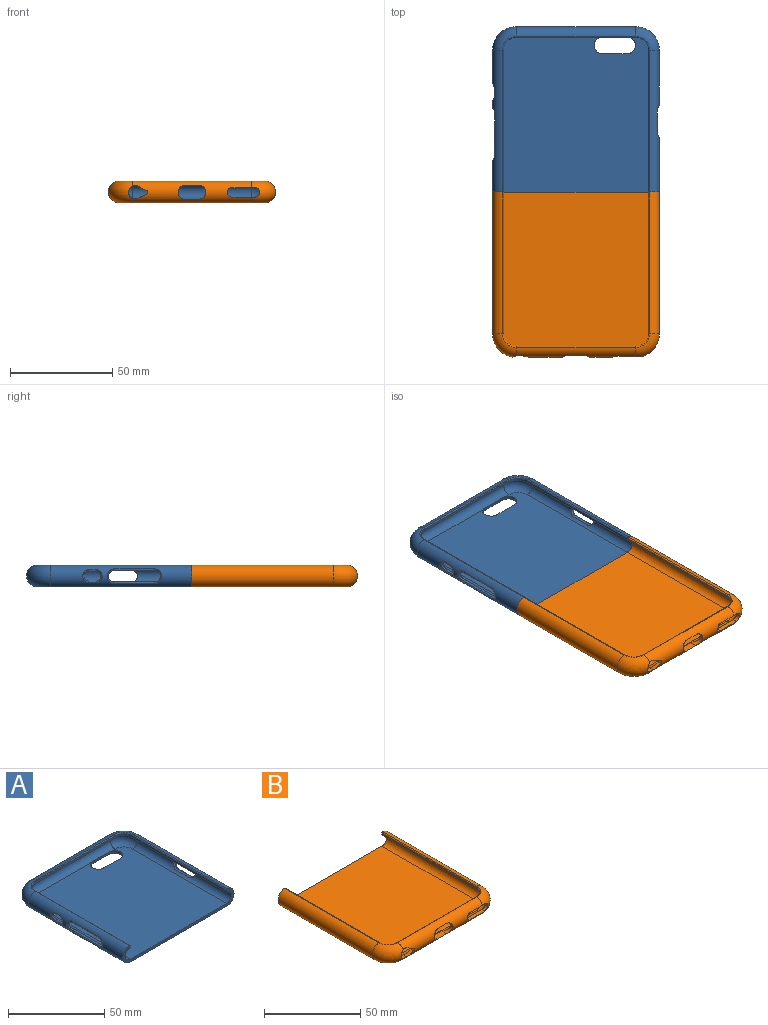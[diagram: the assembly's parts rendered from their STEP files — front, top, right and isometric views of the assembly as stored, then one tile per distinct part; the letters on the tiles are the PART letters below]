
ASSEMBLY  parts=2 mates=1
PART A: 57 faces, bbox 83.7x82x10.8 mm
  f0: plane 75.67x71.04mm, normal (0,0,1), area 5211.4mm2, adj f1,f3,f10,f11,f14,f19,f20,f21
  f1: cylinder r=3.6mm len=69.3mm, axis (0,-1,0), area 691.3mm2, adj f0,f2,f11,f40,f41,f42,f43,f56
  f2: plane 69.3x1.24mm, normal (-1,0,0), area 86.2mm2, adj f1,f8,f12,f56
  f3: cylinder r=3.6mm len=69.3mm, axis (0,1,0), area 589.9mm2, adj f0,f4,f14,f32,f33,f34,f35,f36
  f4: plane 69.3x1.24mm, normal (1,0,0), area 86.2mm2, adj f3,f9,f15,f56
  f5: cylinder r=5.38mm len=69.3mm, axis (0,-1,0), area 1009.5mm2, adj f7,f8,f16,f44,f45,f46,f47,f56
  f6: cylinder r=5.38mm len=69.3mm, axis (0,1,0), area 875.1mm2, adj f7,f9,f18,f48,f49,f50,f51,f52
  f7: plane 75.67x71.04mm, normal (0,0,-1), area 5193.7mm2, adj f5,f6,f16,f17,f18,f23,f24,f25
  f8: cylinder r=0.51mm len=69.3mm, axis (0,-1,0), area 59mm2, adj f2,f5,f29,f56
  f9: cylinder r=0.51mm len=69.3mm, axis (0,1,0), area 59mm2, adj f4,f6,f31,f56
  f10: cylinder r=3.6mm len=58.3mm, axis (1,0,0), area 654.7mm2, adj f0,f11,f13,f14,f19,f21,f22
  f11: torus R=6.37mm, axis (0,0,-1), area 153.9mm2, adj f0,f1,f10,f12
  f12: cylinder r=6.37mm len=6.37mm, axis (0,0,-1), area 12.4mm2, adj f2,f11,f13,f29
  f13: plane 58.3x1.24mm, normal (0,-1,0), area 72.5mm2, adj f10,f12,f15,f30
  f14: torus R=6.37mm, axis (0,0,-1), area 153.9mm2, adj f0,f3,f10,f15
  f15: cylinder r=6.37mm len=6.37mm, axis (0,0,-1), area 12.4mm2, adj f4,f13,f14,f31
  f16: torus R=6.37mm, axis (0,0,-1), area 254.1mm2, adj f5,f7,f17,f29
  f17: cylinder r=5.38mm len=58.3mm, axis (1,0,0), area 937.7mm2, adj f7,f16,f18,f26,f27,f28,f30
  f18: torus R=6.37mm, axis (0,0,-1), area 254.1mm2, adj f6,f7,f17,f31
  f19: cylinder r=4.1mm len=8.2mm, axis (0,0,1), area 16.3mm2, adj f0,f10,f20,f22,f25,f27
  f20: plane 12.06x1.27mm, normal (0,1,0), area 15.3mm2, adj f0,f19,f21,f23
  f21: cylinder r=4.1mm len=8.2mm, axis (0,0,1), area 16.3mm2, adj f0,f10,f20,f22,f24,f26
  f22: plane 12.06x1.21mm, normal (0,-1,0), area 14.6mm2, adj f10,f19,f21,f28
  f23: cylinder r=0.51mm len=12.06mm, axis (1,0,0), area 9.6mm2, adj f7,f20,f24,f25
  f24: torus R=4.61mm, axis (0,0,-1), area 8.6mm2, adj f7,f21,f23,f26
  f25: torus R=4.61mm, axis (0,0,-1), area 8.6mm2, adj f7,f19,f23,f27
  f26: bspline ~4.35x1.88mm, area 2.3mm2, adj f17,f21,f24,f28
  f27: bspline ~3.58x1.88mm, area 2.3mm2, adj f17,f19,f25,f28
  f28: cylinder r=0.51mm len=12.06mm, axis (1,0,0), area 10.7mm2, adj f17,f22,f26,f27
  f29: torus R=6.88mm, axis (0,0,1), area 8.8mm2, adj f8,f12,f16,f30
  f30: cylinder r=0.51mm len=58.3mm, axis (1,0,0), area 49.6mm2, adj f13,f17,f29,f31
  f31: torus R=6.88mm, axis (0,0,1), area 8.8mm2, adj f9,f15,f18,f30
  f32: cylinder r=2.39mm len=4.77mm, axis (1,0,0), area 9.3mm2, adj f3,f33,f35,f55
  f33: plane 3.63x1.2mm, normal (0,0,-1), area 4.4mm2, adj f3,f32,f34,f53
  f34: cylinder r=2.39mm len=4.77mm, axis (1,0,0), area 9.3mm2, adj f3,f33,f35,f52
  f35: plane 3.63x1.25mm, normal (0,0,1), area 4.5mm2, adj f3,f32,f34,f54
  f36: cylinder r=2.8mm len=5.59mm, axis (1,0,0), area 11.2mm2, adj f3,f37,f39,f51
  f37: plane 20.01x1.27mm, normal (0,0,-1), area 25.4mm2, adj f3,f36,f38,f49
  f38: cylinder r=2.8mm len=5.59mm, axis (1,0,0), area 11.2mm2, adj f3,f37,f39,f48
  f39: plane 20.01x1.36mm, normal (0,0,1), area 27.3mm2, adj f3,f36,f38,f50
  f40: plane 10.2x1.27mm, normal (0,0,-1), area 12.9mm2, adj f1,f41,f43,f47
  f41: cylinder r=2.79mm len=5.59mm, axis (-1,0,0), area 11.2mm2, adj f1,f40,f42,f46
  f42: plane 10.2x1.36mm, normal (0,0,1), area 13.9mm2, adj f1,f41,f43,f44
  f43: cylinder r=2.79mm len=5.59mm, axis (-1,0,0), area 11.2mm2, adj f1,f40,f42,f45
  f44: cylinder r=0.51mm len=10.2mm, axis (0,-1,0), area 12.2mm2, adj f5,f42,f45,f46
  f45: bspline ~7.29x3.93mm, area 9.7mm2, adj f5,f43,f44,f47
  f46: bspline ~7.29x3.95mm, area 9.7mm2, adj f5,f41,f44,f47
  f47: cylinder r=0.51mm len=10.2mm, axis (0,-1,0), area 11.8mm2, adj f5,f40,f45,f46
  f48: bspline ~7.3x3.93mm, area 9.8mm2, adj f6,f38,f49,f50
  f49: cylinder r=0.51mm len=20.01mm, axis (0,1,0), area 23.1mm2, adj f6,f37,f48,f51
  f50: cylinder r=0.51mm len=20.01mm, axis (0,1,0), area 24mm2, adj f6,f39,f48,f51
  f51: bspline ~7.3x3.96mm, area 9.8mm2, adj f6,f36,f49,f50
  f52: bspline ~6.39x3.47mm, area 8.1mm2, adj f6,f34,f53,f54
  f53: cylinder r=0.51mm len=3.63mm, axis (0,1,0), area 4mm2, adj f6,f33,f52,f55
  f54: cylinder r=0.51mm len=3.63mm, axis (0,1,0), area 4.1mm2, adj f6,f35,f52,f55
  f55: bspline ~6.39x3.49mm, area 8.1mm2, adj f6,f32,f53,f54
  f56: plane 81.8x10.73mm, normal (0,-1,0), area 176.3mm2, adj f0,f1,f2,f3,f4,f5,f6,f7
PART B: 35 faces, bbox 83.7x82x10.7 mm
  f0: plane 75.67x71.04mm, normal (0,0,1), area 5358.4mm2, adj f2,f3,f4,f10,f12,f34
  f1: plane 75.67x71.04mm, normal (0,0,-1), area 5358.4mm2, adj f5,f6,f7,f15,f16,f34
  f2: torus R=6.37mm, axis (0,0,-1), area 144.8mm2, adj f0,f3,f12,f14,f26
  f3: cylinder r=3.6mm len=58.3mm, axis (-1,0,0), area 454.7mm2, adj f0,f2,f4,f8,f17,f18,f19,f21
  f4: torus R=6.37mm, axis (0,0,-1), area 136mm2, adj f0,f3,f9,f10,f18,f19,f20
  f5: torus R=6.37mm, axis (0,0,-1), area 245.5mm2, adj f1,f6,f16,f26,f33
  f6: cylinder r=5.38mm len=58.3mm, axis (-1,0,0), area 772.5mm2, adj f1,f5,f7,f17,f18,f19,f21,f22
  f7: torus R=6.37mm, axis (0,0,-1), area 237.1mm2, adj f1,f6,f15,f18,f19,f20,f30
  f8: plane 58.3x1.24mm, normal (0,1,0), area 72.5mm2, adj f3,f9,f14,f31
  f9: cylinder r=6.37mm len=6.37mm, axis (0,0,-1), area 12.4mm2, adj f4,f8,f11,f30
  f10: cylinder r=3.6mm len=69.3mm, axis (0,-1,0), area 783.8mm2, adj f0,f4,f11,f34
  f11: plane 69.3x1.24mm, normal (-1,0,0), area 86.2mm2, adj f9,f10,f29,f34
  f12: cylinder r=3.6mm len=69.3mm, axis (0,1,0), area 783.8mm2, adj f0,f2,f13,f34
  f13: plane 69.3x1.24mm, normal (1,0,0), area 86.2mm2, adj f12,f14,f32,f34
  f14: cylinder r=6.37mm len=6.37mm, axis (0,0,-1), area 12.4mm2, adj f2,f8,f13,f33
  f15: cylinder r=5.38mm len=69.3mm, axis (0,-1,0), area 1131.9mm2, adj f1,f7,f29,f34
  f16: cylinder r=5.38mm len=69.3mm, axis (0,1,0), area 1131.9mm2, adj f1,f5,f32,f34
  f17: cylinder r=2.32mm len=4.65mm, axis (0,1,0), area 14.1mm2, adj f3,f6,f18,f19
  f18: plane 11.25x2.19mm, normal (0,0,-1), area 23mm2, adj f3,f4,f6,f7,f17,f20
  f19: plane 11.25x2.33mm, normal (0,0,1), area 24.5mm2, adj f3,f4,f6,f7,f17,f20
  f20: cylinder r=2.32mm len=4.65mm, axis (0,1,0), area 14.8mm2, adj f4,f7,f18,f19
  f21: plane 6.85x2.7mm, normal (0,0,-1), area 18.5mm2, adj f3,f6,f22,f24
  f22: cylinder r=3.4mm len=6.8mm, axis (0,1,0), area 24.3mm2, adj f3,f6,f21,f23
  f23: plane 6.85x3.63mm, normal (0,0,1), area 24.9mm2, adj f3,f6,f22,f24
  f24: cylinder r=3.4mm len=6.8mm, axis (0,1,0), area 24.3mm2, adj f3,f6,f21,f23
  f25: plane 4.25x3.01mm, normal (-0.43,0,-0.9), area 9.3mm2, adj f3,f6,f26,f28
  f26: cylinder r=3.25mm len=6.5mm, axis (0,1,0), area 30.1mm2, adj f2,f3,f5,f6,f25,f27
  f27: plane 4.25x3.46mm, normal (-0.43,0,0.9), area 9.8mm2, adj f3,f6,f26,f28
  f28: cylinder r=1mm len=1.94mm, axis (0,1,0), area 4mm2, adj f3,f6,f25,f27
  f29: cylinder r=0.51mm len=69.3mm, axis (0,-1,0), area 59mm2, adj f11,f15,f30,f34
  f30: torus R=6.88mm, axis (0,0,1), area 8.8mm2, adj f7,f9,f29,f31
  f31: cylinder r=0.51mm len=58.3mm, axis (-1,0,0), area 49.6mm2, adj f6,f8,f30,f33
  f32: cylinder r=0.51mm len=69.3mm, axis (0,1,0), area 59mm2, adj f13,f16,f33,f34
  f33: torus R=6.88mm, axis (0,0,1), area 8.8mm2, adj f5,f14,f31,f32
  f34: plane 81.8x10.73mm, normal (0,1,0), area 176.3mm2, adj f0,f1,f10,f11,f12,f13,f15,f16
PLACE A t=(-27.94,13.25,-14.16)mm
PLACE B t=(-27.94,13.25,-14.16)mm
MATE fastened A.f56 <-> B.f34  axis (0,-1,0) through (-27.94,13.25,-14.91)mm
